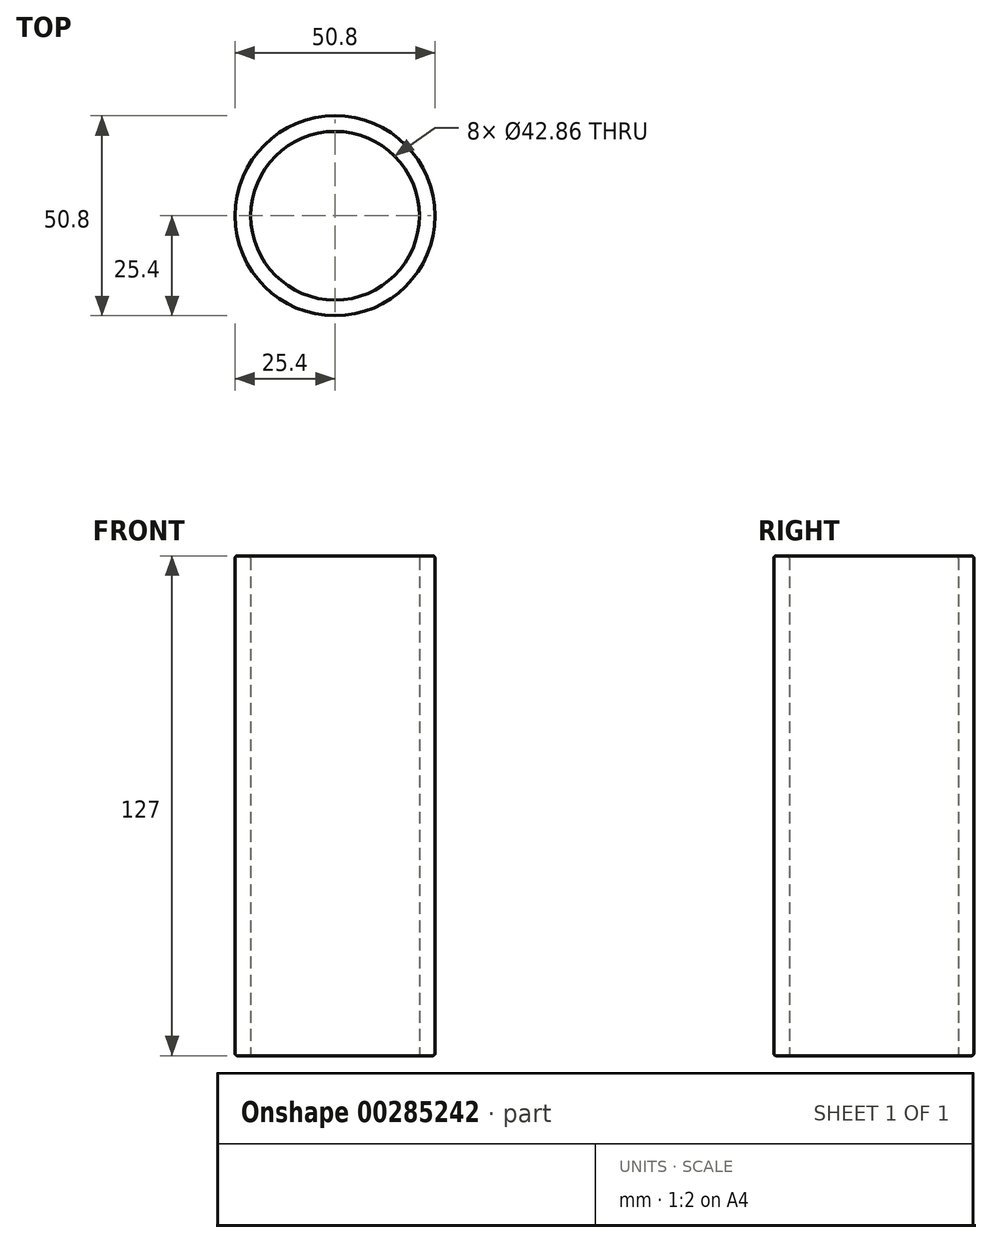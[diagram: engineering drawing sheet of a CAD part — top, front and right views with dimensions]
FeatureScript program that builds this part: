
annotation { "Feature Type Name" : "Feature", "Feature Type Description" : "" }
export const myFeature = defineFeature(function(context is Context, id is Id, definition is map)
    precondition{}
    {
        {
            var Q0;
            Q0=qCreatedBy(makeId("Top.planeOp"),FACE);
            var sketch = newSketch(context, id + "F0", { "sketchPlane" : qUnion([Q0])});
            skCircle(sketch, "E0", {"center": v(0, 0) * mm, "radius": 25.4 * mm});
            skCircle(sketch, "E1", {"center": v(0, 0) * mm, "radius": 21.43 * mm});
            skSolve(sketch);
        }
        {
            var Q0;
            Q0 = qSketchRegion(id + "F0", true);
            extrude(context, id + "F1", {"entities" : qUnion([Q0]), "depth" : 127 * mm});
        }
        {
            var Q0;
            Q0=makeQuery(id+"F1.opExtrude","CAP_EDGE",EDGE,{"disambiguationData":[OSD([sQuery(id+"F0.wireOp",EDGE,"E0")])],"isStart":true});
            var Q1;
            Q1=makeQuery(id+"F1.opExtrude","CAP_EDGE",EDGE,{"disambiguationData":[OSD([sQuery(id+"F0.wireOp",EDGE,"E0")])],"isStart":false});
            var Q2;
            Q2=makeQuery(id+"F1.opExtrude","CAP_EDGE",EDGE,{"disambiguationData":[OSD([sQuery(id+"F0.wireOp",EDGE,"E1")])],"isStart":false});
            var Q3;
            Q3=makeQuery(id+"F1.opExtrude","CAP_EDGE",EDGE,{"disambiguationData":[OSD([sQuery(id+"F0.wireOp",EDGE,"E1")])],"isStart":true});
            fillet(context, id + "F2", {"entities" : qUnion([Q0, Q1, Q2, Q3]), "radius" : 0.64 * mm, "tangentPropagation" : true, "allowEdgeOverflow" : false});
        }
    });
